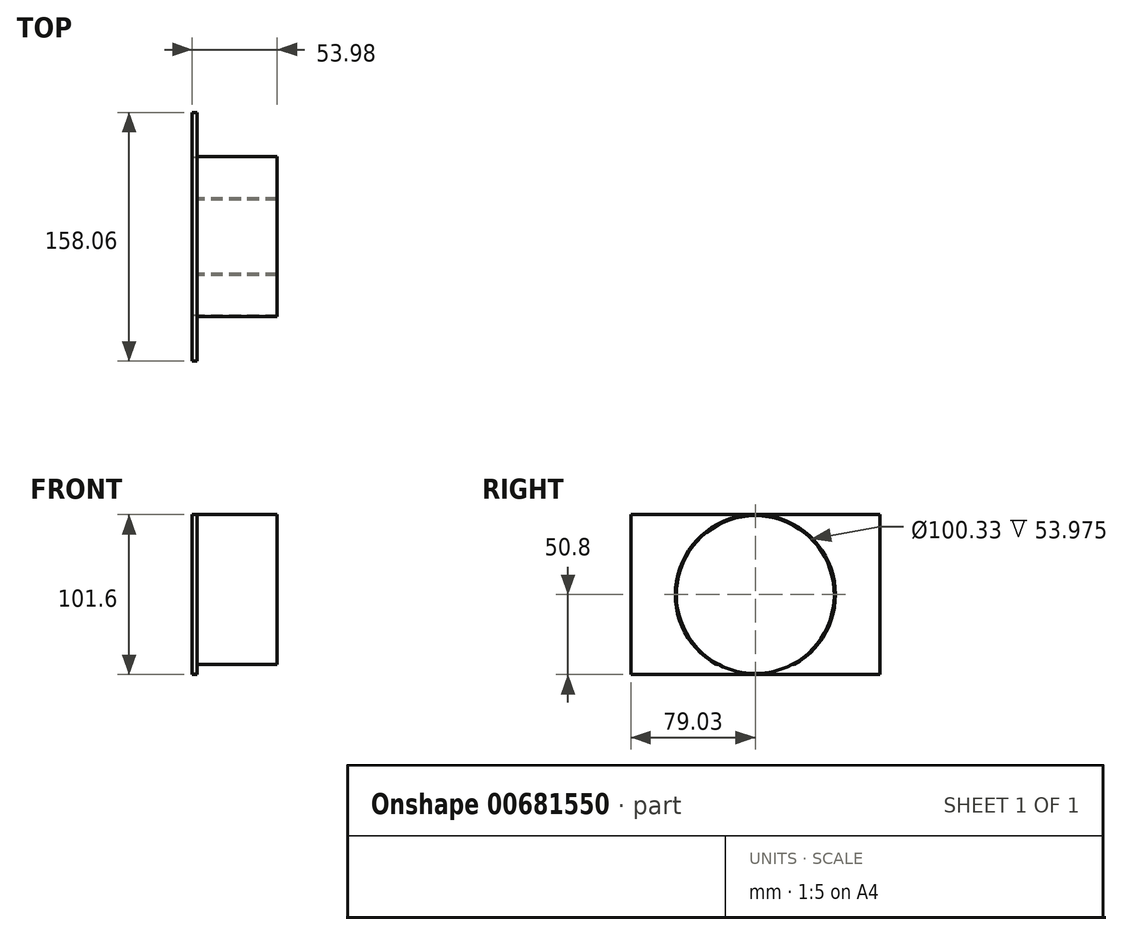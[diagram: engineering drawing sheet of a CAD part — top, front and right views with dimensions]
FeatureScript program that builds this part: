
annotation { "Feature Type Name" : "Feature", "Feature Type Description" : "" }
export const myFeature = defineFeature(function(context is Context, id is Id, definition is map)
    precondition{}
    {
        {
            var Q0;
            Q0=qCreatedBy(makeId("Right.planeOp"),FACE);
            var sketch = newSketch(context, id + "F0", { "sketchPlane" : qUnion([Q0])});
            skLineSegment(sketch, "E0.bottom", {"start": v(79.03, 50.8) * mm, "end": v(-79.03, 50.8) * mm});
            skLineSegment(sketch, "E0.top", {"start": v(79.03, -50.8) * mm, "end": v(-79.03, -50.8) * mm});
            skLineSegment(sketch, "E0.left", {"start": v(79.03, 50.8) * mm, "end": v(79.03, -50.8) * mm});
            skLineSegment(sketch, "E0.right", {"start": v(-79.03, 50.8) * mm, "end": v(-79.03, -50.8) * mm});
            skPoint(sketch, "E0.middle", {"position": v(0, 0) * mm});
            skCircle(sketch, "E1", {"center": v(0, 0) * mm, "radius": 50.17 * mm});
            skSolve(sketch);
        }
        {
            var Q0;
            Q0 = qSketchRegion(id + "F0", true);
            extrude(context, id + "F1", {"entities" : qUnion([Q0]), "depth" : 3.17 * mm, "offsetDistance" : 25.4 * mm});
        }
        {
            var Q0;
            Q0=makeQuery(id+"F1.opExtrude","CAP_FACE",FACE,{"disambiguationData":[OSD([sQuery(id+"F0.wireOp",EDGE,"E0.bottom"),sQuery(id+"F0.wireOp",EDGE,"E0.top"),sQuery(id+"F0.wireOp",EDGE,"E0.left"),sQuery(id+"F0.wireOp",EDGE,"E0.right")])],"isStart":false});
            var sketch = newSketch(context, id + "F2", { "sketchPlane" : qUnion([Q0])});
            skCircle(sketch, "E2", {"center": v(0, 0) * mm, "radius": 50.8 * mm});
            skCircle(sketch, "E3.0", {"center": v(0, 0) * mm, "radius": 49.21 * mm});
            skLineSegment(sketch, "E4.0", {"start": v(-72.68, -44.45) * mm, "end": v(72.68, -44.45) * mm});
            skLineSegment(sketch, "E4.1", {"start": v(-72.68, 44.45) * mm, "end": v(-72.68, -44.45) * mm});
            skLineSegment(sketch, "E4.2", {"start": v(72.68, 44.45) * mm, "end": v(-72.68, 44.45) * mm});
            skLineSegment(sketch, "E4.3", {"start": v(72.68, -44.45) * mm, "end": v(72.68, 44.45) * mm});
            skSolve(sketch);
        }
        {
            var Q0;
            {var subQ0=sQuery(id+"F2.wireOp",EDGE,"E4.2");var subQ1=sQuery(id+"F2.wireOp",EDGE,"E2");var subQ2=makeQuery(id+"F2.imprint","INTERSECT",VERTEX,{"disambiguationData":[OD(1.0)],"derivedFrom":[subQ1,subQ0]});Q0=makeQuery(id+"F2.imprint","IMPRINT",FACE,{"disambiguationData":[TD([[makeQuery(id+"F2.imprint","IMPRINT",EDGE,{"disambiguationData":[TD([[subQ2,-1.0]])],"derivedFrom":subQ1}),1.0]])]});}
            var Q1;
            {var subQ0=sQuery(id+"F2.wireOp",EDGE,"E4.2");var subQ1=sQuery(id+"F2.wireOp",EDGE,"E2");var subQ2=makeQuery(id+"F2.imprint","INTERSECT",VERTEX,{"disambiguationData":[OD(0.0)],"derivedFrom":[subQ1,subQ0]});Q1=makeQuery(id+"F2.imprint","IMPRINT",FACE,{"disambiguationData":[TD([[makeQuery(id+"F2.imprint","IMPRINT",EDGE,{"disambiguationData":[TD([[subQ2,1.0]])],"derivedFrom":subQ1}),1.0]])]});}
            var Q2;
            {var subQ0=sQuery(id+"F2.wireOp",EDGE,"E4.2");var subQ1=sQuery(id+"F2.wireOp",EDGE,"E2");var subQ2=makeQuery(id+"F2.imprint","INTERSECT",VERTEX,{"disambiguationData":[OD(0.0)],"derivedFrom":[subQ1,subQ0]});Q2=makeQuery(id+"F2.imprint","IMPRINT",FACE,{"disambiguationData":[TD([[makeQuery(id+"F2.imprint","IMPRINT",EDGE,{"disambiguationData":[TD([[subQ2,-1.0]])],"derivedFrom":subQ1}),1.0]])]});}
            var Q3;
            {var subQ0=sQuery(id+"F2.wireOp",EDGE,"E4.0");var subQ1=sQuery(id+"F2.wireOp",EDGE,"E2");var subQ2=makeQuery(id+"F2.imprint","INTERSECT",VERTEX,{"disambiguationData":[OD(0.0)],"derivedFrom":[subQ1,subQ0]});Q3=makeQuery(id+"F2.imprint","IMPRINT",FACE,{"disambiguationData":[TD([[makeQuery(id+"F2.imprint","IMPRINT",EDGE,{"disambiguationData":[TD([[subQ2,-1.0]])],"derivedFrom":subQ1}),1.0]])]});}
            extrude(context, id + "F3", {"entities" : qUnion([Q0, Q1, Q2, Q3]), "operationType" : NewBodyOperationType.ADD, "depth" : 50.8 * mm, "offsetDistance" : 25.4 * mm});
        }
    });
